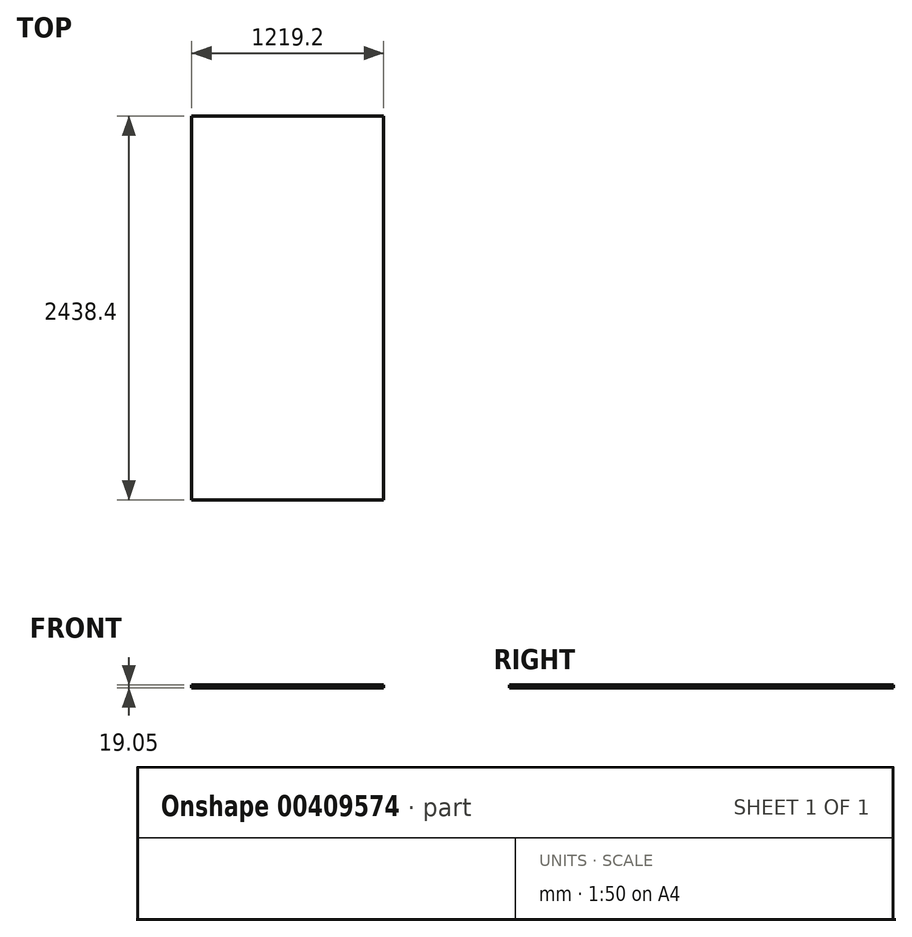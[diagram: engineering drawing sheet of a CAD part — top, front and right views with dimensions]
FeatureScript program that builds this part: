
annotation { "Feature Type Name" : "Feature", "Feature Type Description" : "" }
export const myFeature = defineFeature(function(context is Context, id is Id, definition is map)
    precondition{}
    {
        {
            var Q0;
            Q0=qCreatedBy(makeId("Top.planeOp"),FACE);
            var sketch = newSketch(context, id + "F0", { "sketchPlane" : qUnion([Q0])});
            skLineSegment(sketch, "E0.bottom", {"start": v(-634.47, 1976.16) * mm, "end": v(584.73, 1976.16) * mm});
            skLineSegment(sketch, "E0.top", {"start": v(-634.47, -462.24) * mm, "end": v(584.73, -462.24) * mm});
            skLineSegment(sketch, "E0.left", {"start": v(-634.47, 1976.16) * mm, "end": v(-634.47, -462.24) * mm});
            skLineSegment(sketch, "E0.right", {"start": v(584.73, 1976.16) * mm, "end": v(584.73, -462.24) * mm});
            skSolve(sketch);
        }
        {
            var Q0;
            Q0=makeQuery(id+"F0.imprint","IMPRINT",FACE,{"disambiguationData":[TD([[makeQuery(id+"F0.imprint","IMPRINT",EDGE,{"derivedFrom":sQuery(id+"F0.wireOp",EDGE,"E0.bottom")}),-1.0]])]});
            extrude(context, id + "F1", {"entities" : qUnion([Q0]), "depth" : 19.05 * mm});
        }
    });
